# Revit family: Electronics_Configurable-Audio-DSP_Biamp_Tesira_Server__
name_source: partatom
category: Communication Devices
units: mm (PartAtom-declared; Revit-internal decimal feet)

## family parameters
Cut with Voids When Loaded = No
Host = Face
Maintain Annotation Orientation = No
OmniClass Number = 23.85.10.17.11
OmniClass Title = Audio-Visual System Components
Part Type = Normal
Room Calculation Point = No
Round Connector Dimension = Use Diameter
Shared = No

## types (1)
- SERVER
    A/D Converters = 24-bit
    Apparent Load = 150 VA
    Compliance = FCC Part 15B (USA), FCC Part 68 (USA), Industry Canada CS-03 (Canada), CE marked (Europe), UL and C-UL listed (USA & Canada). RCM (Australia), EAC (Eurasian Customs Union), RoHS Directive (Europe)
    Connector Description = 100-240VAC 50/60Hz
    Cross Talk = 0dB Gain, +4dBu In: < -85dB; 54dB Gain, -50dBu In: < -75dB
    Default Elevation = 48 "
    Depth = 17 "
    Description = Tesira® SERVER Configurable I/O DSP
    Dynamic Range = >108dB
    EIN = <-125dBu
    Frequency Response = +0/-0.25dB
    Height = 5.25 "
    Housing Material = Biamp - Metal - Silver
    Input Gain Range = 6dB Steps: 0 - 66dB
    Input Impedance = 8 kohm
    Manufacturer = Biamp
    Max Power Consumption = 150 W
    Maximum Output = +24dBu
    Model = Tesira SERVER
    Number of Poles = 1
    Output Impedance = 200 ohm
    Phantom Power = +48 VDC (7mA/input)
    Power Factor = 1
    Product Documentation Link = https://downloads.biamp.com
    Product Page URL = https://www.biamp.com
    Product data url = https://www.bimobject.com
    SERVER = Yes
    SERVER-IO = No
    Sampling Rate = 48kHz
    URL = https://www.biamp.com
    Voltage = 120 V
    Weight = 18.00 lbf
    Width = 19 "

## geometry (parser evidence)
native form markers: Sweep x2
no freeform markers — native parametric forms only
